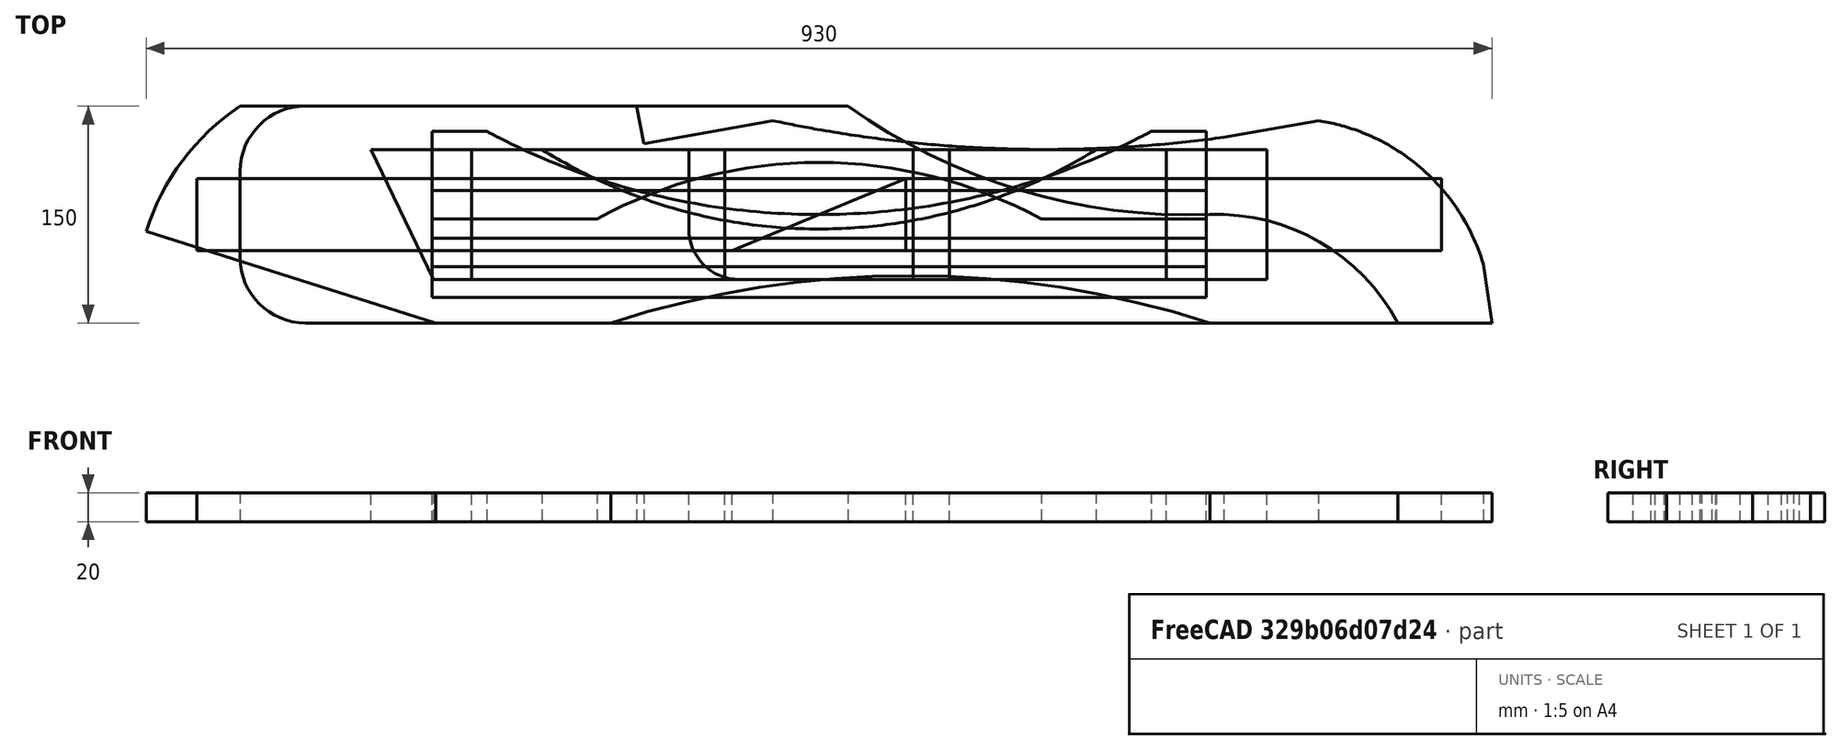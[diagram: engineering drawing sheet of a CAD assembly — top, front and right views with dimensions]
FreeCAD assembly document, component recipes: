
FREECAD ASSEMBLY — COMPONENT RECIPES ("Adirondack Chair")

This assembly document has 28 components, labeled P0..P27 below (a component is one placed body or linked part). 24 of them carry a construction recipe — the FreeCAD feature program that regenerates the part from scratch, quoted from this document or its linked companion documents; the rest are supplied as boundary geometry only. No exploded tour is included for this assembly.
COMPONENT P0 — recipe-attached ("base 1", modeled in this document).
Construction recipe (the document's own serialized feature program — sketch geometry with constraints, then the solid features built on it; lengths are millimeters unless a unit is written):

FEATURE [Sketcher::SketchObject] Sketch
  FullyConstrained = true
  MapMode = 5
  Support = -> [XY_Plane]
  sketch-geometry (5):
    g0: LineSegment StartX=-465 StartY=75 StartZ=0 EndX=-465 EndY=-75 EndZ=0
    g1: LineSegment StartX=-465 StartY=-75 StartZ=0 EndX=465 EndY=-75 EndZ=0
    g2: LineSegment StartX=465 StartY=-75 StartZ=0 EndX=465 EndY=75 EndZ=0
    g3: LineSegment StartX=465 StartY=75 StartZ=0 EndX=-465 EndY=75 EndZ=0
    g4: GeomPoint X=0 Y=0 Z=0
  constraints (12):
    c: Coincident(g0,g1)
    c: Coincident(g1,g2)
    c: Coincident(g2,g3)
    c: Coincident(g3,g0)
    c: Horizontal(g1)
    c: Horizontal(g3)
    c: Vertical(g0)
    c: Vertical(g2)
    c: Symmetric(g1,g0,g4)
    c: Coincident(g4,g-1)
    c: DistanceY(g0,g0) = 150
    c: DistanceX(g3,g3) = 930
FEATURE [PartDesign::Pad] Pad
  Direction = (0,0,1)
  Length = 20
  Length2 = 10
  Profile = -> Sketch
  ReferenceAxis = -> Sketch [N_Axis]
  Type = 0
FEATURE [Sketcher::SketchObject] Sketch001
  ExternalGeometry = -> [Pad]
  FullyConstrained = true
  MapMode = 5
  Placement = pos=(0,0,20) rot=(0,0,1;0rad)
  Support = -> [Pad]
  sketch-geometry (25):
    g0: LineSegment StartX=-265 StartY=-75 StartZ=0 EndX=-465 EndY=-11.5 EndZ=0
    g1: ArcOfCircle CenterX=-309.054 CenterY=-61.0128 CenterZ=0 NormalX=0 NormalY=0 NormalZ=1 AngleXU=0 Radius=163.617 StartAngle=2.16018 EndAngle=2.83416
    g2: LineSegment StartX=-126 StartY=75 StartZ=0 EndX=-121 EndY=49 EndZ=0
    g3: LineSegment StartX=-121 StartY=49 StartZ=0 EndX=-32 EndY=65 EndZ=0
    g4: ArcOfCircle CenterX=323.333 CenterY=-75 CenterZ=0 NormalX=0 NormalY=0 NormalZ=1 AngleXU=0 Radius=141.667 StartAngle=0 EndAngle=1.41725
    g5: LineSegment StartX=-465 StartY=45 StartZ=0 EndX=465 EndY=45 EndZ=0
    g6: LineSegment StartX=-400 StartY=75 StartZ=0 EndX=-465 EndY=75 EndZ=0
    g7: LineSegment StartX=-465 StartY=75 StartZ=0 EndX=-465 EndY=-75 EndZ=0
    g8: LineSegment StartX=-465 StartY=-75 StartZ=0 EndX=-265 EndY=-75 EndZ=0
    g9: LineSegment StartX=-126 StartY=75 StartZ=0 EndX=465 EndY=75 EndZ=0
    g10: LineSegment StartX=465 StartY=75 StartZ=0 EndX=465 EndY=-75 EndZ=0
    g11: ArcOfCircle CenterX=156.5 CenterY=943.306 CenterZ=0 NormalX=0 NormalY=0 NormalZ=1 AngleXU=0 Radius=898.306 StartAngle=4.50098 EndAngle=4.53588
    g12: ArcOfCircle CenterX=156.5 CenterY=943.306 CenterZ=0 NormalX=0 NormalY=0 NormalZ=1 AngleXU=0 Radius=898.306 StartAngle=4.53588 EndAngle=4.58824
    g13: ArcOfCircle CenterX=156.5 CenterY=943.306 CenterZ=0 NormalX=0 NormalY=0 NormalZ=1 AngleXU=0 Radius=898.306 StartAngle=4.58824 EndAngle=4.9238
    g14: ArcOfCircle CenterX=156.5 CenterY=943.306 CenterZ=0 NormalX=0 NormalY=0 NormalZ=1 AngleXU=0 Radius=898.306 StartAngle=4.58824 EndAngle=4.6406
    g15: ArcOfCircle CenterX=156.5 CenterY=943.306 CenterZ=0 NormalX=0 NormalY=0 NormalZ=1 AngleXU=0 Radius=898.306 StartAngle=4.6406 EndAngle=4.69296
    g16: ArcOfCircle CenterX=156.5 CenterY=943.306 CenterZ=0 NormalX=0 NormalY=0 NormalZ=1 AngleXU=0 Radius=898.306 StartAngle=4.69296 EndAngle=4.74532
    g17: ArcOfCircle CenterX=156.5 CenterY=943.306 CenterZ=0 NormalX=0 NormalY=0 NormalZ=1 AngleXU=0 Radius=898.306 StartAngle=4.74532 EndAngle=4.79768
    g18: ArcOfCircle CenterX=156.5 CenterY=943.306 CenterZ=0 NormalX=0 NormalY=0 NormalZ=1 AngleXU=0 Radius=898.306 StartAngle=4.79768 EndAngle=4.85004
    g19: LineSegment StartX=279.766 StartY=53.4976 StartZ=0 EndX=345 EndY=65 EndZ=0
    g20: ArcOfCircle CenterX=323.333 CenterY=-75 CenterZ=0 NormalX=0 NormalY=0 NormalZ=1 AngleXU=0 Radius=141.667 StartAngle=1.20781 EndAngle=1.41725
    g21: ArcOfCircle CenterX=323.333 CenterY=-75 CenterZ=0 NormalX=0 NormalY=0 NormalZ=1 AngleXU=0 Radius=141.667 StartAngle=0.90238 EndAngle=1.20781
    g22: ArcOfCircle CenterX=323.333 CenterY=-75 CenterZ=0 NormalX=0 NormalY=0 NormalZ=1 AngleXU=0 Radius=141.667 StartAngle=0.596948 EndAngle=0.90238
    g23: ArcOfCircle CenterX=323.333 CenterY=-75 CenterZ=0 NormalX=0 NormalY=0 NormalZ=1 AngleXU=0 Radius=141.667 StartAngle=0.291515 EndAngle=0.596948
    g24: LineSegment StartX=459.023 StartY=-34.2845 StartZ=0 EndX=465 EndY=-75 EndZ=0
  constraints (71):
    c: PointOnObject(g0,g-3)
    c: Perpendicular(g0,g1) = 1.5708
    c: Coincident(g2,g3)
    c: DistanceX(g-3,g0) = 200
    c: DistanceY(g-3,g0) = 63.5
    c: DistanceX(g1,g2) = 274
    c: DistanceX(g2,g2) = 5
    c: DistanceY(g2,g2) = 26
    c: DistanceY(g3,g2) = 10
    c: DistanceX(g-3,g1) = 65
    c: Horizontal(g3,g4)
    c: Horizontal(g-3,g1)
    c: DistanceX(g4,g-4) = 120
    c: DistanceX(g2,g3) = 89
    c: Horizontal(g5)
    c: DistanceY(g5,g3) = 20
    c: PointOnObject(g5,g-4)
    c: PointOnObject(g5,g-3)
    c: Tangent(g4,g-4) = -1.5708
    c: Coincident(g1,g6)
    c: Coincident(g6,g7)
    c: Coincident(g7,g-3)
    c: Coincident(g7,g8)
    c: Coincident(g8,g0)
    c: Horizontal(g8)
    c: Coincident(g6,g-3)
    c: Coincident(g2,g9)
    c: Coincident(g9,g-4)
    c: Horizontal(g9)
    c: Coincident(g9,g10)
    c: Coincident(g10,g4)
    c: Coincident(g11,g3)
    c: Angle(g11) = 0.0349066
    c: Coincident(g12,g11)
    c: Coincident(g12,g11)
    c: Angle(g12) = 0.0523599
    c: Coincident(g13,g11)
    c: Coincident(g13,g12)
    c: Coincident(g13,g4)
    c: Tangent(g13,g5)
    c: Coincident(g14,g11)
    c: Coincident(g14,g12)
    c: Coincident(g15,g11)
    c: Coincident(g15,g14)
    c: Angle(g14) = 0.0523599
    c: Angle(g15) = 0.0523599
    c: Coincident(g16,g11)
    c: Coincident(g16,g15)
    c: Angle(g16) = 0.0523599
    c: Coincident(g17,g11)
    c: Coincident(g17,g16)
    c: Angle(g17) = 0.0523599
    c: Coincident(g18,g11)
    c: Coincident(g18,g17)
    c: Angle(g18) = 0.0523599
    c: Coincident(g19,g18)
    c: Coincident(g19,g4)
    c: Coincident(g20,g4)
    c: Coincident(g20,g19)
    c: Coincident(g21,g20)
    c: Coincident(g21,g20)
    c: Angle(g20) = 0.20944
    c: Angle(g21) = 0.305433
    c: Coincident(g22,g20)
    c: Coincident(g22,g21)
    c: Angle(g22) = 0.305433
    c: Coincident(g23,g20)
    c: Coincident(g23,g22)
    c: Angle(g23) = 0.305433
    c: Coincident(g24,g23)
    c: Coincident(g24,g10)
FEATURE [PartDesign::Pocket] Pocket
  BaseFeature = -> Pad
  Direction = (0,0,-1)
  Length = 5
  Length2 = 5
  Profile = -> Sketch001
  ReferenceAxis = -> Sketch001 [N_Axis]
  Type = 1
FEATURE [PartDesign::Body] Body  label="base"
  Group = -> [Sketch,Pad,Sketch001,Pocket]
  Origin = -> Origin
  Tip = -> Pocket
COMPONENT P1 — same part as P0; its construction recipe is shown at P0.
COMPONENT P2 — recipe-attached ("suporte_encosto001", modeled in this document).
Construction recipe (the document's own serialized feature program — sketch geometry with constraints, then the solid features built on it; lengths are millimeters unless a unit is written):

FEATURE [PartDesign::ShapeBinder] ShapeBinder
  Support = -> [Sketch008]
  TraceSupport = false
FEATURE [Sketcher::SketchObject] Sketch009
  ExternalGeometry = -> [ShapeBinder]
  FullyConstrained = true
  MapMode = 5
  Support = -> [XY_Plane008]
  sketch-geometry (5):
    g0: LineSegment StartX=-267.5 StartY=45 StartZ=0 EndX=-267.5 EndY=-45 EndZ=0
    g1: LineSegment StartX=-267.5 StartY=-45 StartZ=0 EndX=267.5 EndY=-45 EndZ=0
    g2: LineSegment StartX=267.5 StartY=-45 StartZ=0 EndX=267.5 EndY=45 EndZ=0
    g3: LineSegment StartX=267.5 StartY=45 StartZ=0 EndX=-267.5 EndY=45 EndZ=0
    g4: GeomPoint X=-2e-16 Y=0 Z=0
  constraints (12):
    c: Coincident(g0,g1)
    c: Coincident(g1,g2)
    c: Coincident(g2,g3)
    c: Coincident(g3,g0)
    c: Horizontal(g1)
    c: Horizontal(g3)
    c: Vertical(g0)
    c: Vertical(g2)
    c: Symmetric(g1,g0,g4)
    c: Coincident(g4,g-1)
    c: DistanceY(g0,g0) = 90
    c: Equal(g3,g-3)
FEATURE [PartDesign::Pad] Pad008
  Direction = (0,0,1)
  Length = 20
  Length2 = 10
  Profile = -> Sketch009
  ReferenceAxis = -> Sketch009 [N_Axis]
  Type = 0
FEATURE [Sketcher::SketchObject] Sketch014
  ExternalGeometry = -> [Pad008]
  FullyConstrained = true
  MapMode = 5
  Placement = pos=(0,0,20) rot=(0,0,1;0rad)
  Support = -> [Pad008]
  sketch-geometry (10):
    g0: LineSegment StartX=-191.5 StartY=45 StartZ=0 EndX=191.5 EndY=45 EndZ=0
    g1: LineSegment StartX=-267.5 StartY=-10 StartZ=0 EndX=267.5 EndY=-10 EndZ=0
    g2: ArcOfCircle CenterX=-2.96e-14 CenterY=350.884 CenterZ=0 NormalX=0 NormalY=0 NormalZ=1 AngleXU=0 Radius=360.884 StartAngle=4.71239 EndAngle=4.85015
    g3: ArcOfCircle CenterX=-2.96e-14 CenterY=350.884 CenterZ=0 NormalX=0 NormalY=0 NormalZ=1 AngleXU=0 Radius=360.884 StartAngle=4.85015 EndAngle=4.98792
    g4: ArcOfCircle CenterX=-2.96e-14 CenterY=350.884 CenterZ=0 NormalX=0 NormalY=0 NormalZ=1 AngleXU=0 Radius=360.884 StartAngle=4.98792 EndAngle=5.12569
    g5: ArcOfCircle CenterX=-2.96e-14 CenterY=350.884 CenterZ=0 NormalX=0 NormalY=0 NormalZ=1 AngleXU=0 Radius=360.884 StartAngle=5.12569 EndAngle=5.27175
    g6: ArcOfCircle CenterX=-2.96e-14 CenterY=350.884 CenterZ=0 NormalX=0 NormalY=0 NormalZ=1 AngleXU=0 Radius=360.884 StartAngle=4.15303 EndAngle=4.2908
    g7: ArcOfCircle CenterX=-2.96e-14 CenterY=350.884 CenterZ=0 NormalX=0 NormalY=0 NormalZ=1 AngleXU=0 Radius=360.884 StartAngle=4.2908 EndAngle=4.42856
    g8: ArcOfCircle CenterX=-2.96e-14 CenterY=350.884 CenterZ=0 NormalX=0 NormalY=0 NormalZ=1 AngleXU=0 Radius=360.884 StartAngle=4.42856 EndAngle=4.56633
    g9: ArcOfCircle CenterX=-2.96e-14 CenterY=350.884 CenterZ=0 NormalX=0 NormalY=0 NormalZ=1 AngleXU=0 Radius=360.884 StartAngle=4.56633 EndAngle=4.71239
  constraints (31):
    c: PointOnObject(g0,g-3)
    c: Symmetric(g0,g0,g-2)
    c: DistanceX(g0,g-3) = 76
    c: Horizontal(g1)
    c: Vertical(g1,g-4)
    c: Vertical(g1,g-4)
    c: DistanceY(g-4,g1) = 35
    c: PointOnObject(g2,g1)
    c: PointOnObject(g2,g-2)
    c: Coincident(g3,g2)
    c: Coincident(g3,g2)
    c: Coincident(g4,g2)
    c: Coincident(g4,g3)
    c: Coincident(g5,g2)
    c: Coincident(g5,g4)
    c: Coincident(g5,g0)
    c: Angle(g2) = 0.137766
    c: Angle(g3) = 0.137766
    c: Angle(g4) = 0.137766
    c: Coincident(g6,g2)
    c: Coincident(g6,g0)
    c: Coincident(g7,g2)
    c: Coincident(g7,g6)
    c: Coincident(g8,g2)
    c: Coincident(g8,g7)
    c: Coincident(g9,g2)
    c: Coincident(g9,g8)
    c: Coincident(g9,g2)
    c: Angle(g6) = 0.137766
    c: Angle(g7) = 0.137766
    c: Angle(g8) = 0.137766
FEATURE [PartDesign::Pocket] Pocket002
  BaseFeature = -> Pad008
  Direction = (0,0,-1)
  Length = 5
  Length2 = 5
  Profile = -> Sketch014
  ReferenceAxis = -> Sketch014 [N_Axis]
  Type = 1
FEATURE [PartDesign::Body] Body008  label="suporte_encosto"
  Group = -> [Sketch009,Pad008,Sketch014,Pocket002,ShapeBinder]
  Origin = -> Origin008
  Tip = -> Pocket002
COMPONENT P3 — recipe-attached ("ripa_curvada001", modeled in this document).
Construction recipe (the document's own serialized feature program — sketch geometry with constraints, then the solid features built on it; lengths are millimeters unless a unit is written):

FEATURE [PartDesign::ShapeBinder] ShapeBinder001
  Support = -> [Sketch008]
  TraceSupport = false
FEATURE [Sketcher::SketchObject] Sketch010
  ExternalGeometry = -> [ShapeBinder001]
  FullyConstrained = true
  MapMode = 5
  Support = -> [XY_Plane009]
  sketch-geometry (5):
    g0: LineSegment StartX=-267.5 StartY=-36 StartZ=0 EndX=-267.5 EndY=36 EndZ=0
    g1: LineSegment StartX=-267.5 StartY=36 StartZ=0 EndX=267.5 EndY=36 EndZ=0
    g2: LineSegment StartX=267.5 StartY=36 StartZ=0 EndX=267.5 EndY=-36 EndZ=0
    g3: LineSegment StartX=267.5 StartY=-36 StartZ=0 EndX=-267.5 EndY=-36 EndZ=0
    g4: GeomPoint X=-1e-16 Y=0 Z=0
  constraints (12):
    c: Coincident(g0,g1)
    c: Coincident(g1,g2)
    c: Coincident(g2,g3)
    c: Coincident(g3,g0)
    c: Horizontal(g1)
    c: Horizontal(g3)
    c: Vertical(g0)
    c: Vertical(g2)
    c: Symmetric(g1,g0,g4)
    c: Coincident(g4,g-1)
    c: DistanceY(g0,g0) = 72
    c: Equal(g1,g-3)
FEATURE [PartDesign::Pad] Pad009
  Direction = (0,0,1)
  Length = 20
  Length2 = 10
  Profile = -> Sketch010
  ReferenceAxis = -> Sketch010 [N_Axis]
  Type = 0
FEATURE [Sketcher::SketchObject] Sketch013
  ExternalGeometry = -> [Pad009]
  FullyConstrained = true
  MapMode = 5
  Placement = pos=(0,0,20) rot=(0,0,1;0rad)
  Support = -> [Pad009]
  sketch-geometry (6):
    g0: LineSegment StartX=-153.5 StartY=-3 StartZ=0 EndX=-267.5 EndY=-3 EndZ=0
    g1: LineSegment StartX=-267.5 StartY=-3 StartZ=0 EndX=-267.5 EndY=36 EndZ=0
    g2: LineSegment StartX=-267.5 StartY=36 StartZ=0 EndX=267.5 EndY=36 EndZ=0
    g3: LineSegment StartX=267.5 StartY=36 StartZ=0 EndX=267.5 EndY=-3 EndZ=0
    g4: LineSegment StartX=267.5 StartY=-3 StartZ=0 EndX=153.5 EndY=-3 EndZ=0
    g5: ArcOfCircle CenterX=2.9e-14 CenterY=-285.58 CenterZ=0 NormalX=0 NormalY=0 NormalZ=1 AngleXU=0 Radius=321.58 StartAngle=1.07318 EndAngle=2.06841
  constraints (17):
    c: Coincident(g0,g1)
    c: Coincident(g1,g-3)
    c: Vertical(g1)
    c: Coincident(g1,g2)
    c: Coincident(g2,g-3)
    c: Coincident(g2,g3)
    c: Vertical(g3)
    c: Equal(g3,g1)
    c: DistanceY(g-4,g3) = 33
    c: Coincident(g3,g4)
    c: Horizontal(g4)
    c: Equal(g0,g4)
    c: DistanceX(g4,g4) = 114
    c: Coincident(g5,g0)
    c: Coincident(g5,g4)
    c: Tangent(g5,g2)
    c: Horizontal(g0)
FEATURE [PartDesign::Pocket] Pocket001
  BaseFeature = -> Pad009
  Direction = (0,0,-1)
  Length = 5
  Length2 = 5
  Profile = -> Sketch013
  ReferenceAxis = -> Sketch013 [N_Axis]
  Type = 1
FEATURE [PartDesign::Body] Body009  label="ripa_curvada"
  Group = -> [Sketch010,Pad009,Sketch013,Pocket001,ShapeBinder001]
  Origin = -> Origin009
  Tip = -> Pocket001
COMPONENT P4 — recipe-attached ("ripa001", modeled in this document).
Construction recipe (the document's own serialized feature program — sketch geometry with constraints, then the solid features built on it; lengths are millimeters unless a unit is written):

FEATURE [Sketcher::SketchObject] Sketch008
  FullyConstrained = true
  MapMode = 5
  Support = -> [XY_Plane007]
  sketch-geometry (5):
    g0: LineSegment StartX=-267.5 StartY=16.5 StartZ=0 EndX=-267.5 EndY=-16.5 EndZ=0
    g1: LineSegment StartX=-267.5 StartY=-16.5 StartZ=0 EndX=267.5 EndY=-16.5 EndZ=0
    g2: LineSegment StartX=267.5 StartY=-16.5 StartZ=0 EndX=267.5 EndY=16.5 EndZ=0
    g3: LineSegment StartX=267.5 StartY=16.5 StartZ=0 EndX=-267.5 EndY=16.5 EndZ=0
    g4: GeomPoint X=0 Y=0 Z=0
  constraints (12):
    c: Coincident(g0,g1)
    c: Coincident(g1,g2)
    c: Coincident(g2,g3)
    c: Coincident(g3,g0)
    c: Horizontal(g1)
    c: Horizontal(g3)
    c: Vertical(g0)
    c: Vertical(g2)
    c: Symmetric(g1,g0,g4)
    c: Coincident(g4,g-1)
    c: DistanceY(g0,g0) = 33
    c: DistanceX(g3,g3) = 535
FEATURE [PartDesign::Pad] Pad007
  Direction = (0,0,1)
  Length = 20
  Length2 = 10
  Profile = -> Sketch008
  ReferenceAxis = -> Sketch008 [N_Axis]
  Type = 0
FEATURE [PartDesign::Body] Body007  label="ripa"
  Group = -> [Sketch008,Pad007]
  Origin = -> Origin007
  Tip = -> Pad007
COMPONENT P5 — same part as P4; its construction recipe is shown at P4.
COMPONENT P6 — same part as P4; its construction recipe is shown at P4.
COMPONENT P7 — same part as P4; its construction recipe is shown at P4.
COMPONENT P8 — same part as P4; its construction recipe is shown at P4.
COMPONENT P9 — same part as P4; its construction recipe is shown at P4.
COMPONENT P10 — same part as P4; its construction recipe is shown at P4.
COMPONENT P11 — same part as P4; its construction recipe is shown at P4.
COMPONENT P12 — same part as P4; its construction recipe is shown at P4.
COMPONENT P13 — same part as P4; its construction recipe is shown at P4.
COMPONENT P14 — same part as P4; its construction recipe is shown at P4.
COMPONENT P15 — same part as P4; its construction recipe is shown at P4.
COMPONENT P16 — recipe-attached ("pe001", modeled in this document).
Construction recipe (the document's own serialized feature program — sketch geometry with constraints, then the solid features built on it; lengths are millimeters unless a unit is written):

FEATURE [Sketcher::SketchObject] Sketch002
  FullyConstrained = true
  MapMode = 5
  Support = -> [XY_Plane001]
  sketch-geometry (5):
    g0: LineSegment StartX=-240 StartY=45 StartZ=0 EndX=-240 EndY=-45 EndZ=0
    g1: LineSegment StartX=-240 StartY=-45 StartZ=0 EndX=240 EndY=-45 EndZ=0
    g2: LineSegment StartX=240 StartY=-45 StartZ=0 EndX=240 EndY=45 EndZ=0
    g3: LineSegment StartX=240 StartY=45 StartZ=0 EndX=-240 EndY=45 EndZ=0
    g4: GeomPoint X=0 Y=0 Z=0
  constraints (12):
    c: Coincident(g0,g1)
    c: Coincident(g1,g2)
    c: Coincident(g2,g3)
    c: Coincident(g3,g0)
    c: Horizontal(g1)
    c: Horizontal(g3)
    c: Vertical(g0)
    c: Vertical(g2)
    c: Symmetric(g1,g0,g4)
    c: Coincident(g4,g-1)
    c: DistanceY(g0,g0) = 90
    c: DistanceX(g3,g3) = 480
FEATURE [PartDesign::Pad] Pad001
  Direction = (0,0,1)
  Length = 20
  Length2 = 10
  Profile = -> Sketch002
  ReferenceAxis = -> Sketch002 [N_Axis]
  Type = 0
FEATURE [PartDesign::Body] Body001  label="pe"
  Group = -> [Sketch002,Pad001]
  Origin = -> Origin001
  Tip = -> Pad001
COMPONENT P17 — same part as P16; its construction recipe is shown at P16.
COMPONENT P18 — recipe-attached ("suporte_bracos001", modeled in this document).
Construction recipe (the document's own serialized feature program — sketch geometry with constraints, then the solid features built on it; lengths are millimeters unless a unit is written):

FEATURE [Sketcher::SketchObject] Sketch003
  FullyConstrained = true
  MapMode = 5
  Support = -> [XY_Plane002]
  sketch-geometry (5):
    g0: LineSegment StartX=-65 StartY=45 StartZ=0 EndX=-65 EndY=-45 EndZ=0
    g1: LineSegment StartX=-65 StartY=-45 StartZ=0 EndX=65 EndY=-45 EndZ=0
    g2: LineSegment StartX=65 StartY=-45 StartZ=0 EndX=65 EndY=45 EndZ=0
    g3: LineSegment StartX=65 StartY=45 StartZ=0 EndX=-65 EndY=45 EndZ=0
    g4: GeomPoint X=0 Y=0 Z=0
  constraints (12):
    c: Coincident(g0,g1)
    c: Coincident(g1,g2)
    c: Coincident(g2,g3)
    c: Coincident(g3,g0)
    c: Horizontal(g1)
    c: Horizontal(g3)
    c: Vertical(g0)
    c: Vertical(g2)
    c: Symmetric(g1,g0,g4)
    c: Coincident(g4,g-1)
    c: DistanceY(g0,g0) = 90
    c: DistanceX(g3,g3) = 130
FEATURE [PartDesign::Pad] Pad002
  Direction = (0,0,1)
  Length = 20
  Length2 = 10
  Profile = -> Sketch003
  ReferenceAxis = -> Sketch003 [N_Axis]
  Type = 0
FEATURE [PartDesign::Body] Body002  label="suporte_bracos"
  Group = -> [Sketch003,Pad002]
  Origin = -> Origin002
  Tip = -> Pad002
COMPONENT P19 — same part as P18; its construction recipe is shown at P18.
COMPONENT P20 — recipe-attached ("mao_francesa001", modeled in this document).
Construction recipe (the document's own serialized feature program — sketch geometry with constraints, then the solid features built on it; lengths are millimeters unless a unit is written):

FEATURE [Sketcher::SketchObject] Sketch004
  FullyConstrained = true
  MapMode = 5
  Support = -> [XY_Plane003]
  sketch-geometry (5):
    g0: LineSegment StartX=-90 StartY=45 StartZ=0 EndX=-90 EndY=-45 EndZ=0
    g1: LineSegment StartX=-90 StartY=-45 StartZ=0 EndX=90 EndY=-45 EndZ=0
    g2: LineSegment StartX=90 StartY=-45 StartZ=0 EndX=90 EndY=45 EndZ=0
    g3: LineSegment StartX=90 StartY=45 StartZ=0 EndX=-90 EndY=45 EndZ=0
    g4: GeomPoint X=0 Y=0 Z=0
  constraints (12):
    c: Coincident(g0,g1)
    c: Coincident(g1,g2)
    c: Coincident(g2,g3)
    c: Coincident(g3,g0)
    c: Horizontal(g1)
    c: Horizontal(g3)
    c: Vertical(g0)
    c: Vertical(g2)
    c: Symmetric(g1,g0,g4)
    c: Coincident(g4,g-1)
    c: DistanceY(g0,g0) = 90
    c: DistanceX(g3,g3) = 180
FEATURE [PartDesign::Pad] Pad003
  Direction = (0,0,1)
  Length = 20
  Length2 = 10
  Profile = -> Sketch004
  ReferenceAxis = -> Sketch004 [N_Axis]
  Type = 0
FEATURE [PartDesign::Fillet] Fillet001
  Base = -> Pad003 [Edge2]
  BaseFeature = -> Pad003
  Radius = 35
  SupportTransform = false
  UseAllEdges = false
FEATURE [PartDesign::Body] Body003  label="mao_francesa"
  Group = -> [Sketch004,Pad003,Fillet001]
  Origin = -> Origin003
  Tip = -> Fillet001
COMPONENT P21 — same part as P20; its construction recipe is shown at P20.
COMPONENT P22 — geometry summary ("pecas002"; no construction recipe available for this part):
  bounding box: 619.0 x 90.0 x 20.0 mm
  tessellated surface: 12 triangles
  volume: 1075500 mm^3 (97% of its bounding box)
  symmetry: mirror-symmetric across its y mid-plane
COMPONENT P23 — recipe-attached ("suporte_superior001", modeled in this document).
Construction recipe (the document's own serialized feature program — sketch geometry with constraints, then the solid features built on it; lengths are millimeters unless a unit is written):

FEATURE [PartDesign::ShapeBinder] ShapeBinder002
  Support = -> [Sketch008]
  TraceSupport = false
FEATURE [Sketcher::SketchObject] Sketch011
  ExternalGeometry = -> [ShapeBinder002]
  FullyConstrained = true
  MapMode = 5
  Support = -> [XY_Plane010]
  sketch-geometry (5):
    g0: LineSegment StartX=-267.5 StartY=57.5 StartZ=0 EndX=-267.5 EndY=-57.5 EndZ=0
    g1: LineSegment StartX=-267.5 StartY=-57.5 StartZ=0 EndX=267.5 EndY=-57.5 EndZ=0
    g2: LineSegment StartX=267.5 StartY=-57.5 StartZ=0 EndX=267.5 EndY=57.5 EndZ=0
    g3: LineSegment StartX=267.5 StartY=57.5 StartZ=0 EndX=-267.5 EndY=57.5 EndZ=0
    g4: GeomPoint X=2e-16 Y=0 Z=0
  constraints (12):
    c: Coincident(g0,g1)
    c: Coincident(g1,g2)
    c: Coincident(g2,g3)
    c: Coincident(g3,g0)
    c: Horizontal(g1)
    c: Horizontal(g3)
    c: Vertical(g0)
    c: Vertical(g2)
    c: Symmetric(g1,g0,g4)
    c: Coincident(g4,g-1)
    c: DistanceY(g0,g0) = 115
    c: Equal(g3,g-3)
FEATURE [PartDesign::Pad] Pad010
  Direction = (0,0,1)
  Length = 20
  Length2 = 10
  Profile = -> Sketch011
  ReferenceAxis = -> Sketch011 [N_Axis]
  Type = 0
FEATURE [Sketcher::SketchObject] Sketch016
  ExternalGeometry = -> [Pad010]
  FullyConstrained = true
  MapMode = 5
  Placement = pos=(0,0,20) rot=(0,0,1;0rad)
  Support = -> [Pad010]
  sketch-geometry (9):
    g0: LineSegment StartX=-229.5 StartY=57.5 StartZ=0 EndX=229.5 EndY=57.5 EndZ=0
    g1: ArcOfCircle CenterX=5.49e-14 CenterY=486.752 CenterZ=0 NormalX=0 NormalY=0 NormalZ=1 AngleXU=0 Radius=486.752 StartAngle=4.71239 EndAngle=4.86947
    g2: ArcOfCircle CenterX=5.49e-14 CenterY=486.752 CenterZ=0 NormalX=0 NormalY=0 NormalZ=1 AngleXU=0 Radius=486.752 StartAngle=4.86947 EndAngle=5.02655
    g3: ArcOfCircle CenterX=5.49e-14 CenterY=486.752 CenterZ=0 NormalX=0 NormalY=0 NormalZ=1 AngleXU=0 Radius=486.752 StartAngle=4.55531 EndAngle=4.71239
    g4: ArcOfCircle CenterX=5.49e-14 CenterY=486.752 CenterZ=0 NormalX=0 NormalY=0 NormalZ=1 AngleXU=0 Radius=486.752 StartAngle=4.39823 EndAngle=4.55531
    g5: ArcOfCircle CenterX=5.49e-14 CenterY=486.752 CenterZ=0 NormalX=0 NormalY=0 NormalZ=1 AngleXU=0 Radius=486.752 StartAngle=5.02655 EndAngle=5.18363
    g6: ArcOfCircle CenterX=5.49e-14 CenterY=486.752 CenterZ=0 NormalX=0 NormalY=0 NormalZ=1 AngleXU=0 Radius=486.752 StartAngle=5.18363 EndAngle=5.20337
    g7: ArcOfCircle CenterX=5.49e-14 CenterY=486.752 CenterZ=0 NormalX=0 NormalY=0 NormalZ=1 AngleXU=0 Radius=486.752 StartAngle=4.24115 EndAngle=4.39823
    g8: ArcOfCircle CenterX=5.49e-14 CenterY=486.752 CenterZ=0 NormalX=0 NormalY=0 NormalZ=1 AngleXU=0 Radius=486.752 StartAngle=4.22141 EndAngle=4.24115
  constraints (26):
    c: PointOnObject(g0,g-3)
    c: Symmetric(g0,g0,g-2)
    c: DistanceX(g0,g-3) = 38
    c: Angle(g1) = 0.15708
    c: Coincident(g2,g1)
    c: Angle(g2) = 0.15708
    c: Coincident(g3,g1)
    c: Coincident(g3,g1)
    c: Coincident(g4,g1)
    c: Coincident(g4,g3)
    c: Angle(g3) = 0.15708
    c: Angle(g4) = 0.15708
    c: Coincident(g2,g1)
    c: Coincident(g1,g-1)
    c: Coincident(g5,g1)
    c: Coincident(g5,g2)
    c: Coincident(g6,g1)
    c: Coincident(g6,g5)
    c: Coincident(g6,g0)
    c: Angle(g5) = 0.15708
    c: Coincident(g7,g1)
    c: Coincident(g7,g4)
    c: Coincident(g8,g1)
    c: Coincident(g8,g7)
    c: Coincident(g8,g0)
    c: Angle(g7) = 0.15708
FEATURE [PartDesign::Pocket] Pocket004
  BaseFeature = -> Pad010
  Direction = (0,0,-1)
  Length = 5
  Length2 = 5
  Profile = -> Sketch016
  ReferenceAxis = -> Sketch016 [N_Axis]
  Type = 1
FEATURE [PartDesign::Body] Body010  label="suporte_superior"
  Group = -> [Sketch011,Pad010,Sketch016,Pocket004,ShapeBinder002]
  Origin = -> Origin010
  Tip = -> Pocket004
COMPONENT P24 — recipe-attached ("encosto001", modeled in this document).
Construction recipe (the document's own serialized feature program — sketch geometry with constraints, then the solid features built on it; lengths are millimeters unless a unit is written):

FEATURE [Sketcher::SketchObject] Sketch012
  FullyConstrained = true
  MapMode = 5
  Support = -> [XY_Plane011]
  sketch-geometry (5):
    g0: LineSegment StartX=-430 StartY=25 StartZ=0 EndX=-430 EndY=-25 EndZ=0
    g1: LineSegment StartX=-430 StartY=-25 StartZ=0 EndX=430 EndY=-25 EndZ=0
    g2: LineSegment StartX=430 StartY=-25 StartZ=0 EndX=430 EndY=25 EndZ=0
    g3: LineSegment StartX=430 StartY=25 StartZ=0 EndX=-430 EndY=25 EndZ=0
    g4: GeomPoint X=0 Y=0 Z=0
  constraints (12):
    c: Coincident(g0,g1)
    c: Coincident(g1,g2)
    c: Coincident(g2,g3)
    c: Coincident(g3,g0)
    c: Horizontal(g1)
    c: Horizontal(g3)
    c: Vertical(g0)
    c: Vertical(g2)
    c: Symmetric(g1,g0,g4)
    c: Coincident(g4,g-1)
    c: DistanceY(g0,g0) = 50
    c: DistanceX(g3,g3) = 860
FEATURE [PartDesign::Pad] Pad011
  Direction = (0,0,1)
  Length = 20
  Length2 = 10
  Profile = -> Sketch012
  ReferenceAxis = -> Sketch012 [N_Axis]
  Type = 0
FEATURE [PartDesign::Body] Body011  label="encosto"
  Group = -> [Sketch012,Pad011]
  Origin = -> Origin011
  Tip = -> Pad011
COMPONENT P25 — geometry summary ("encosto007"; no construction recipe available for this part):
  bounding box: 801.3 x 353.0 x 182.0 mm
  tessellated surface: 12 triangles
  volume: 860000 mm^3 (2% of its bounding box)
COMPONENT P26 — geometry summary ("triangulo002"; no construction recipe available for this part):
  bounding box: 120.0 x 50.0 x 20.0 mm
  tessellated surface: 8 triangles
  volume: 60000 mm^3 (50% of its bounding box)
  symmetry: mirror-symmetric across its x mid-plane
COMPONENT P27 — geometry summary ("bracos002"; no construction recipe available for this part):
  bounding box: 800.0 x 150.0 x 20.0 mm
  tessellated surface: 468 triangles
  volume: 1689767 mm^3 (70% of its bounding box)
  symmetry: mirror-symmetric across its z mid-plane
PROVENANCE & LICENSES
A FreeCAD (.FCStd) document from a public repository crawl; recipes are the document's own serialized feature recipes (and, for linked parts, companion documents' recipes).
License: as declared in the source repository (recorded in the dataset sidecar).
